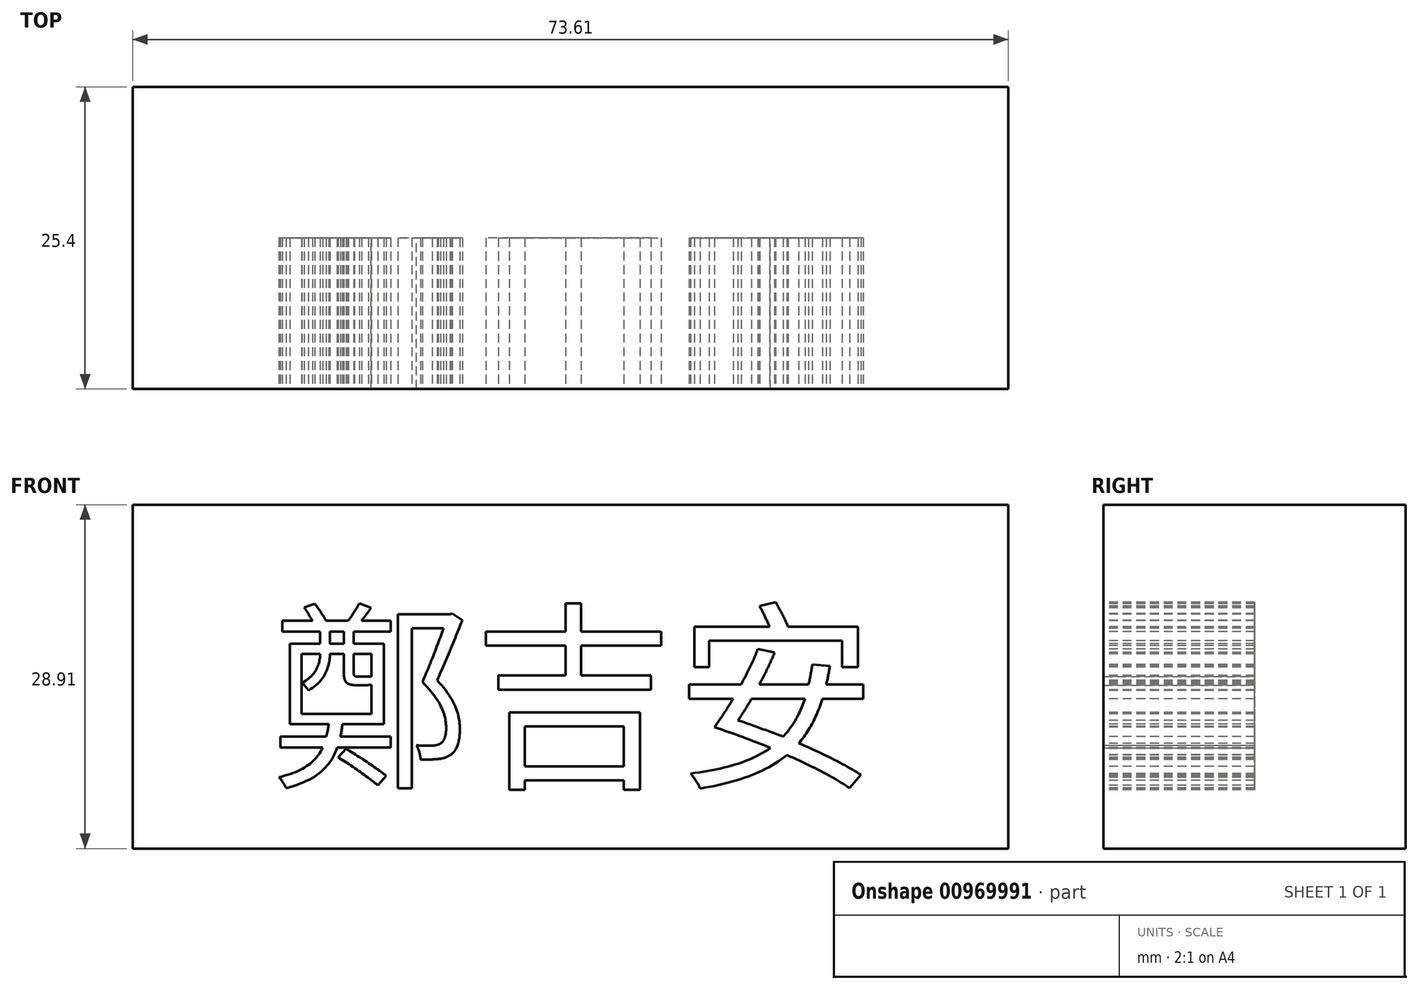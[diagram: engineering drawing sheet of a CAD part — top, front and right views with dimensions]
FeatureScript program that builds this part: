
annotation { "Feature Type Name" : "Feature", "Feature Type Description" : "" }
export const myFeature = defineFeature(function(context is Context, id is Id, definition is map)
    precondition{}
    {
        {
            var Q0;
            Q0=qCreatedBy(makeId("Front.planeOp"),FACE);
            var sketch = newSketch(context, id + "F0", { "sketchPlane" : qUnion([Q0])});
            skText(sketch, "E0", { "text": "鄭吉安", "fontName": "NotoSansCJKtc-Regular.otf"});
            const initialGuessF0  = {"E0": [-0.0266, 0.01123, 1, 0, 0.01225]};
            skSetInitialGuess(sketch, initialGuessF0);
            skSolve(sketch);
        }
        {
            var Q0;
            Q0=qCreatedBy(makeId("Front.planeOp"),FACE);
            var sketch = newSketch(context, id + "F1", { "sketchPlane" : qUnion([Q0])});
            skLineSegment(sketch, "E1.bottom", {"start": v(-38.14, 33.75) * mm, "end": v(35.47, 33.75) * mm});
            skLineSegment(sketch, "E1.top", {"start": v(-38.14, 4.84) * mm, "end": v(35.47, 4.84) * mm});
            skLineSegment(sketch, "E1.left", {"start": v(-38.14, 33.75) * mm, "end": v(-38.14, 4.84) * mm});
            skLineSegment(sketch, "E1.right", {"start": v(35.47, 33.75) * mm, "end": v(35.47, 4.84) * mm});
            skSolve(sketch);
        }
        {
            var Q0;
            Q0 = qSketchRegion(id + "F1", true);
            extrude(context, id + "F2", {"entities" : qUnion([Q0]), "oppositeDirection" : true, "depth" : 25.4 * mm, "offsetDistance" : 25.4 * mm});
        }
        {
            var Q0;
            Q0 = qSketchRegion(id + "F0", true);
            extrude(context, id + "F3", {"entities" : qUnion([Q0]), "operationType" : NewBodyOperationType.REMOVE, "oppositeDirection" : true, "depth" : 12.7 * mm, "offsetDistance" : 25.4 * mm});
        }
    });
